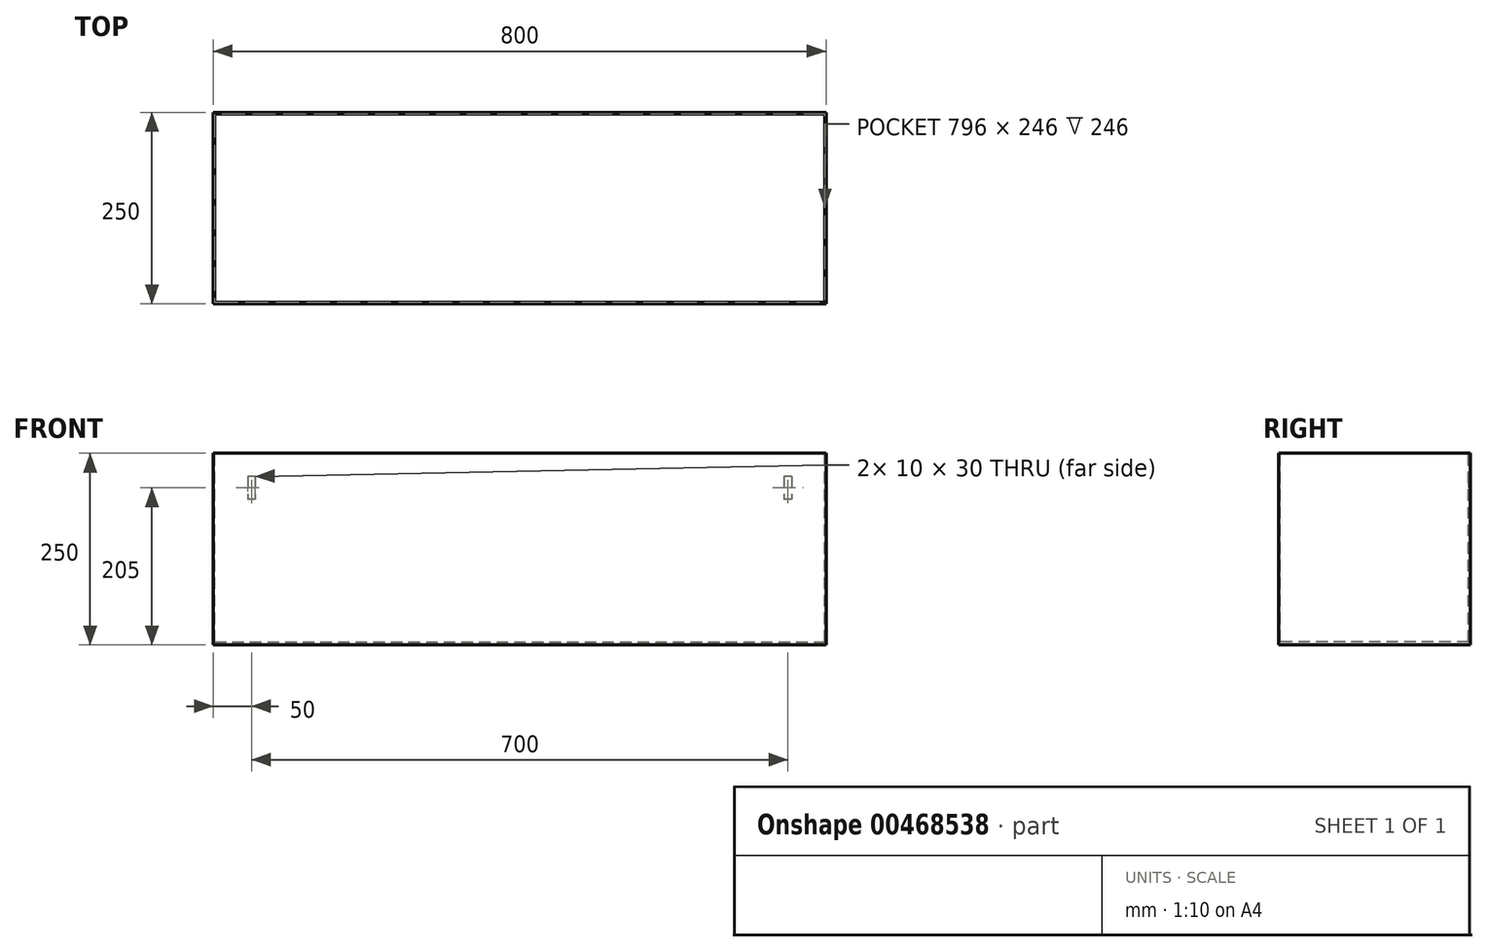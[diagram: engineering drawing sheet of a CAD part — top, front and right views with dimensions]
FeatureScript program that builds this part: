
annotation { "Feature Type Name" : "Feature", "Feature Type Description" : "" }
export const myFeature = defineFeature(function(context is Context, id is Id, definition is map)
    precondition{}
    {
        {
            var Q0;
            Q0=qCreatedBy(makeId("Top.planeOp"),FACE);
            var sketch = newSketch(context, id + "F0", { "sketchPlane" : qUnion([Q0])});
            skLineSegment(sketch, "E0.bottom", {"start": v(-390.88, 84.85) * mm, "end": v(409.12, 84.85) * mm});
            skLineSegment(sketch, "E0.top", {"start": v(-390.88, -165.15) * mm, "end": v(409.12, -165.15) * mm});
            skLineSegment(sketch, "E0.left", {"start": v(-390.88, 84.85) * mm, "end": v(-390.88, -165.15) * mm});
            skLineSegment(sketch, "E0.right", {"start": v(409.12, 84.85) * mm, "end": v(409.12, -165.15) * mm});
            skSolve(sketch);
        }
        {
            var Q0;
            Q0=makeQuery(id+"F0.imprint","IMPRINT",FACE,{"disambiguationData":[TD([[makeQuery(id+"F0.imprint","IMPRINT",EDGE,{"derivedFrom":sQuery(id+"F0.wireOp",EDGE,"E0.bottom")}),-1.0]])]});
            extrude(context, id + "F1", {"entities" : qUnion([Q0]), "depth" : 250 * mm, "offsetDistance" : 25 * mm});
        }
        {
            var Q0;
            Q0=makeQuery(id+"F1.opExtrude","CAP_FACE",FACE,{"disambiguationData":[OSD([sQuery(id+"F0.wireOp",EDGE,"E0.bottom"),sQuery(id+"F0.wireOp",EDGE,"E0.top"),sQuery(id+"F0.wireOp",EDGE,"E0.left"),sQuery(id+"F0.wireOp",EDGE,"E0.right")])],"isStart":false});
            var sketch = newSketch(context, id + "F2", { "sketchPlane" : qUnion([Q0])});
            skLineSegment(sketch, "E1.bottom", {"start": v(-388.88, 82.85) * mm, "end": v(407.12, 82.85) * mm});
            skLineSegment(sketch, "E1.top", {"start": v(-388.88, -163.15) * mm, "end": v(407.12, -163.15) * mm});
            skLineSegment(sketch, "E1.left", {"start": v(-388.88, 82.85) * mm, "end": v(-388.88, -163.15) * mm});
            skLineSegment(sketch, "E1.right", {"start": v(407.12, 82.85) * mm, "end": v(407.12, -163.15) * mm});
            skSolve(sketch);
        }
        {
            var Q0;
            Q0 = qSketchRegion(id + "F2", true);
            extrude(context, id + "F3", {"entities" : qUnion([Q0]), "operationType" : NewBodyOperationType.REMOVE, "oppositeDirection" : true, "depth" : 246 * mm, "offsetDistance" : 25 * mm});
        }
        {
            var Q0;
            Q0=makeQuery(id+"F1.opExtrude","SWEPT_FACE",FACE,{"disambiguationData":[OSD([sQuery(id+"F0.wireOp",EDGE,"E0.bottom")])]});
            var sketch = newSketch(context, id + "F4", { "sketchPlane" : qUnion([Q0])});
            skLineSegment(sketch, "E2", {"start": v(-359.12, 250) * mm, "end": v(-359.12, 0) * mm, "construction": true});
            skLineSegment(sketch, "E3", {"start": v(340.88, 250) * mm, "end": v(340.88, 0) * mm, "construction": true});
            skLineSegment(sketch, "E4.bottom", {"start": v(-364.12, 220) * mm, "end": v(-354.12, 220) * mm});
            skLineSegment(sketch, "E4.top", {"start": v(-364.12, 190) * mm, "end": v(-354.12, 190) * mm});
            skLineSegment(sketch, "E4.left", {"start": v(-364.12, 220) * mm, "end": v(-364.12, 190) * mm});
            skLineSegment(sketch, "E4.right", {"start": v(-354.12, 220) * mm, "end": v(-354.12, 190) * mm});
            skPoint(sketch, "E5", {"position": v(-359.12, 220) * mm});
            skLineSegment(sketch, "E6.bottom", {"start": v(335.88, 220) * mm, "end": v(345.88, 220) * mm});
            skLineSegment(sketch, "E6.top", {"start": v(335.88, 190) * mm, "end": v(345.88, 190) * mm});
            skLineSegment(sketch, "E6.left", {"start": v(335.88, 220) * mm, "end": v(335.88, 190) * mm});
            skLineSegment(sketch, "E6.right", {"start": v(345.88, 220) * mm, "end": v(345.88, 190) * mm});
            skPoint(sketch, "E7", {"position": v(340.88, 220) * mm});
            skSolve(sketch);
        }
        {
            var Q0;
            Q0=makeQuery(id+"F4.imprint","IMPRINT",FACE,{"disambiguationData":[TD([[makeQuery(id+"F4.imprint","IMPRINT",EDGE,{"derivedFrom":sQuery(id+"F4.wireOp",EDGE,"E4.bottom")}),-1.0]])]});
            var Q1;
            Q1=makeQuery(id+"F4.imprint","IMPRINT",FACE,{"disambiguationData":[TD([[makeQuery(id+"F4.imprint","IMPRINT",EDGE,{"derivedFrom":sQuery(id+"F4.wireOp",EDGE,"E6.bottom")}),-1.0]])]});
            extrude(context, id + "F5", {"entities" : qUnion([Q0, Q1]), "operationType" : NewBodyOperationType.REMOVE, "endBound" : BoundingType.UP_TO_NEXT, "oppositeDirection" : true, "depth" : 25 * mm, "offsetDistance" : 25 * mm});
        }
    });
